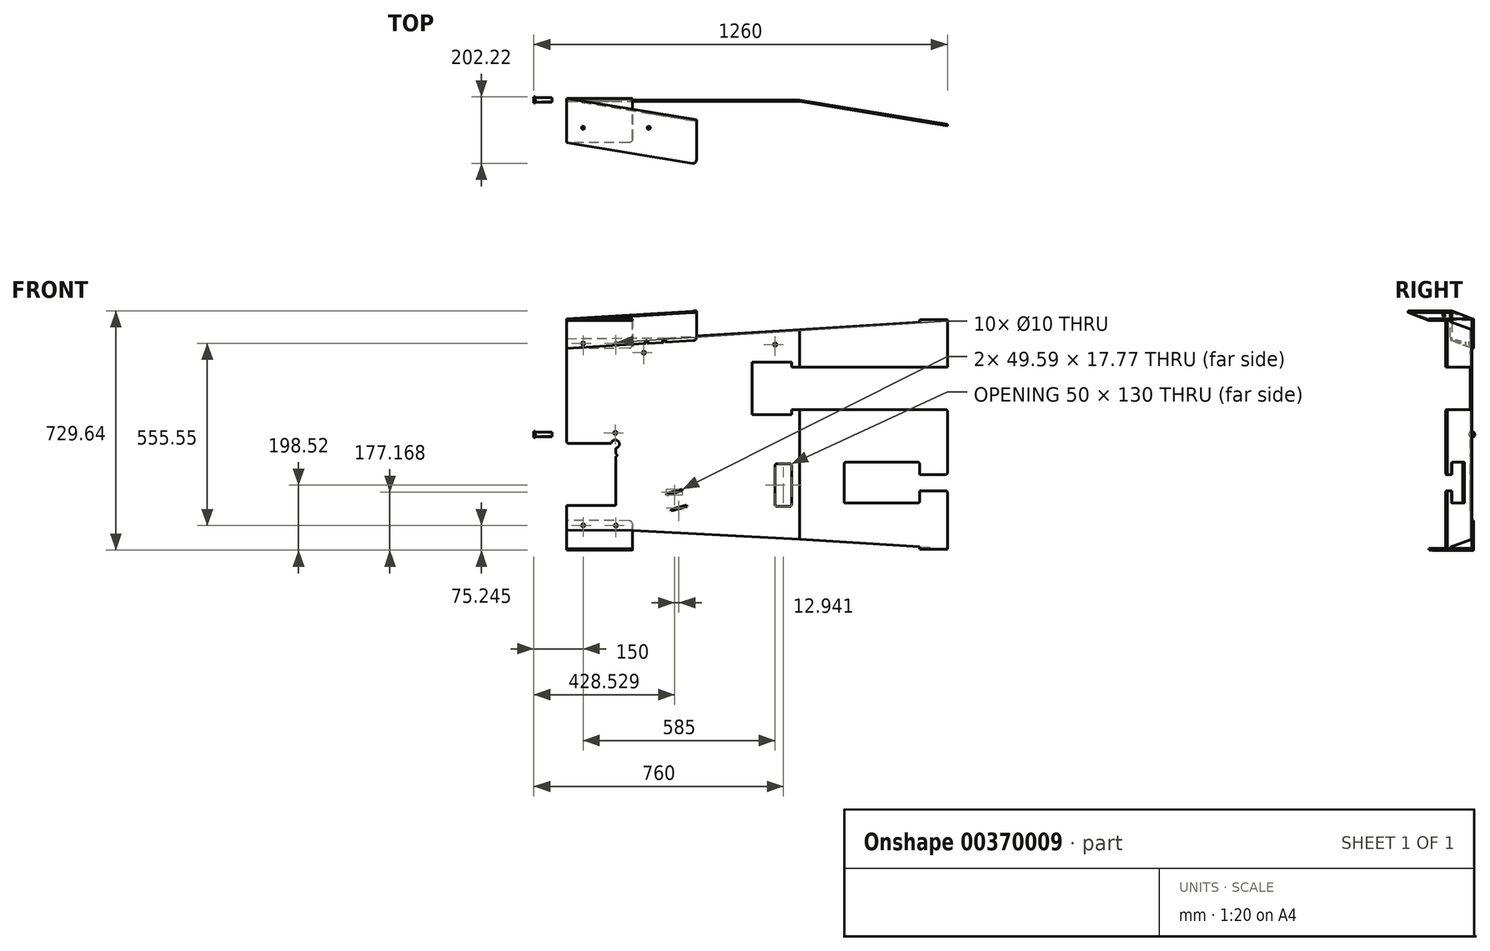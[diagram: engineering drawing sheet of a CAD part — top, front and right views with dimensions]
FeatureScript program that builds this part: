
annotation { "Feature Type Name" : "Feature", "Feature Type Description" : "" }
export const myFeature = defineFeature(function(context is Context, id is Id, definition is map)
    precondition{}
    {
        {
            var Q0;
            Q0=qCreatedBy(makeId("Front.planeOp"),FACE);
            var sketch = newSketch(context, id + "F0", { "sketchPlane" : qUnion([Q0])});
            skLineSegment(sketch, "E0", {"start": v(0, 0) * mm, "end": v(1170, 0) * mm});
            skLineSegment(sketch, "E1", {"start": v(0, 0) * mm, "end": v(0, 292) * mm});
            skPoint(sketch, "E2", {"position": v(200, 0) * mm});
            skLineSegment(sketch, "E3", {"start": v(200, 0) * mm, "end": v(200, 293) * mm});
            skPoint(sketch, "E4", {"position": v(199, 0) * mm});
            skPoint(sketch, "E5", {"position": v(302, 0) * mm});
            skLineSegment(sketch, "E6", {"start": v(302, 0) * mm, "end": v(302, 294.5) * mm});
            skPoint(sketch, "E7", {"position": v(432, 0) * mm});
            skLineSegment(sketch, "E8", {"start": v(432, 0) * mm, "end": v(432, 302.5) * mm});
            skPoint(sketch, "E9", {"position": v(565, 0) * mm});
            skLineSegment(sketch, "E10", {"start": v(565, 0) * mm, "end": v(565, 311) * mm});
            skPoint(sketch, "E11", {"position": v(710, 0) * mm});
            skLineSegment(sketch, "E12", {"start": v(710, 0) * mm, "end": v(710, 319.5) * mm});
            skPoint(sketch, "E13", {"position": v(1160, 0) * mm});
            skLineSegment(sketch, "E14", {"start": v(1160, 0) * mm, "end": v(1160, 347.5) * mm});
            skLineSegment(sketch, "E15", {"start": v(0, 292) * mm, "end": v(302, 294.5) * mm});
            skLineSegment(sketch, "E16", {"start": v(302, 294.5) * mm, "end": v(710, 319.5) * mm});
            skLineSegment(sketch, "E17", {"start": v(710, 319.5) * mm, "end": v(1160, 347.5) * mm});
            skLineSegment(sketch, "E18.MirrorCS", {"start": v(1160, 0) * mm, "end": v(1160, -347.5) * mm});
            skLineSegment(sketch, "E19.MirrorCS", {"start": v(710, 0) * mm, "end": v(710, -319.5) * mm});
            skLineSegment(sketch, "E20.MirrorCS", {"start": v(565, 0) * mm, "end": v(565, -311) * mm});
            skLineSegment(sketch, "E21.MirrorCS", {"start": v(432, 0) * mm, "end": v(432, -302.5) * mm});
            skLineSegment(sketch, "E22.MirrorCS", {"start": v(302, 0) * mm, "end": v(302, -294.5) * mm});
            skLineSegment(sketch, "E23.MirrorCS", {"start": v(200, 0) * mm, "end": v(200, -293) * mm});
            skLineSegment(sketch, "E24.MirrorCS", {"start": v(0, 0) * mm, "end": v(0, -292) * mm});
            skLineSegment(sketch, "E25", {"start": v(0, -292) * mm, "end": v(200, -293) * mm});
            skLineSegment(sketch, "E26", {"start": v(200, -293) * mm, "end": v(710, -319.5) * mm});
            skLineSegment(sketch, "E27", {"start": v(710, -319.5) * mm, "end": v(1160, -347.5) * mm});
            skSolve(sketch);
        }
        {
            var Q0;
            Q0=qCreatedBy(makeId("Front.planeOp"),FACE);
            var sketch = newSketch(context, id + "F1", { "sketchPlane" : qUnion([Q0])});
            skPoint(sketch, "E28", {"position": v(0, -217) * mm});
            skPoint(sketch, "E29", {"position": v(0, -27) * mm});
            skLineSegment(sketch, "E30", {"start": v(0, -27) * mm, "end": v(150, -27) * mm});
            skLineSegment(sketch, "E31", {"start": v(150, -27) * mm, "end": v(150, -217) * mm});
            skLineSegment(sketch, "E32", {"start": v(150, -217) * mm, "end": v(0, -217) * mm});
            skLineSegment(sketch, "E33", {"start": v(0, -27) * mm, "end": v(0, -217) * mm});
            skPoint(sketch, "E34", {"position": v(565, 310.62) * mm});
            skLineSegment(sketch, "E35", {"start": v(565, 220.62) * mm, "end": v(565, 60.62) * mm});
            skLineSegment(sketch, "E36", {"start": v(565, 220.62) * mm, "end": v(685, 220.62) * mm});
            skLineSegment(sketch, "E37", {"start": v(685, 220.62) * mm, "end": v(685, 60.62) * mm});
            skLineSegment(sketch, "E38", {"start": v(685, 60.62) * mm, "end": v(565, 60.62) * mm});
            skLineSegment(sketch, "E39", {"start": v(685, 205.62) * mm, "end": v(1160, 205.62) * mm});
            skLineSegment(sketch, "E40", {"start": v(685, 75.62) * mm, "end": v(1160, 75.62) * mm});
            skLineSegment(sketch, "E41", {"start": v(1160, 205.62) * mm, "end": v(1160, 75.62) * mm});
            skPoint(sketch, "E42", {"position": v(710, -319.5) * mm});
            skPoint(sketch, "E43", {"position": v(685, -219.5) * mm});
            skLineSegment(sketch, "E44.bottom", {"start": v(685, -219.5) * mm, "end": v(635, -219.5) * mm});
            skLineSegment(sketch, "E44.top", {"start": v(685, -89.5) * mm, "end": v(635, -89.5) * mm});
            skLineSegment(sketch, "E44.left", {"start": v(685, -219.5) * mm, "end": v(685, -89.5) * mm});
            skLineSegment(sketch, "E44.right", {"start": v(635, -219.5) * mm, "end": v(635, -89.5) * mm});
            skPoint(sketch, "E45", {"position": v(845, -209.5) * mm});
            skLineSegment(sketch, "E46", {"start": v(845, -209.5) * mm, "end": v(845, -84.5) * mm});
            skLineSegment(sketch, "E47", {"start": v(845, -84.5) * mm, "end": v(1075, -84.5) * mm});
            skLineSegment(sketch, "E48", {"start": v(1075, -84.5) * mm, "end": v(1075, -209.5) * mm});
            skLineSegment(sketch, "E49", {"start": v(1075, -209.5) * mm, "end": v(845, -209.5) * mm});
            skPoint(sketch, "E50", {"position": v(1075, -122) * mm});
            skPoint(sketch, "E51", {"position": v(1075, -147) * mm});
            skLineSegment(sketch, "E52", {"start": v(1075, -122) * mm, "end": v(1075, -172) * mm});
            skLineSegment(sketch, "E53", {"start": v(1075, -172) * mm, "end": v(1160, -172) * mm});
            skLineSegment(sketch, "E54", {"start": v(1160, -172) * mm, "end": v(1160, -122) * mm});
            skLineSegment(sketch, "E55", {"start": v(1160, -122) * mm, "end": v(1075, -122) * mm});
            skSolve(sketch);
        }
        {
            var Q0;
            Q0=qCreatedBy(makeId("Top.planeOp"),FACE);
            var sketch = newSketch(context, id + "F2", { "sketchPlane" : qUnion([Q0])});
            skPoint(sketch, "E56", {"position": v(0, 0) * mm});
            skLineSegment(sketch, "E57.0", {"start": v(302, 0) * mm, "end": v(710, 0) * mm});
            skLineSegment(sketch, "E58", {"start": v(0, 0) * mm, "end": v(710, 0) * mm});
            skLineSegment(sketch, "E59.0", {"start": v(710, 0) * mm, "end": v(1160, 0) * mm});
            skLineSegment(sketch, "E60", {"start": v(0, 0) * mm, "end": v(0, -5) * mm});
            skLineSegment(sketch, "E61", {"start": v(0, -5) * mm, "end": v(710, -5) * mm});
            skLineSegment(sketch, "E62", {"start": v(1160, -5) * mm, "end": v(1160, 0) * mm});
            skPoint(sketch, "E63", {"position": v(1160, -74) * mm});
            skLineSegment(sketch, "E64", {"start": v(1160, -79) * mm, "end": v(1160, -74) * mm});
            skLineSegment(sketch, "E65", {"start": v(710, 0) * mm, "end": v(1160, -74) * mm});
            skLineSegment(sketch, "E66", {"start": v(710, -5) * mm, "end": v(1160, -79) * mm});
            skSolve(sketch);
        }
        {
            var Q0;
            Q0 = qSketchRegion(id + "F2", true);
            extrude(context, id + "F3", {"entities" : qUnion([Q0]), "endBound" : BoundingType.SYMMETRIC, "depth" : 700 * mm});
        }
        {
            var Q0;
            Q0 = qSketchRegion(id + "F1", true);
            extrude(context, id + "F4", {"entities" : qUnion([Q0]), "operationType" : NewBodyOperationType.REMOVE, "depth" : 80 * mm});
        }
        {
            var Q0;
            Q0=qCreatedBy(makeId("Front.planeOp"),FACE);
            var sketch = newSketch(context, id + "F5", { "sketchPlane" : qUnion([Q0])});
            skLineSegment(sketch, "E67.0", {"start": v(0, 292) * mm, "end": v(302, 294.5) * mm});
            skLineSegment(sketch, "E68.0", {"start": v(302, 294.5) * mm, "end": v(710, 319.5) * mm});
            skLineSegment(sketch, "E69.0", {"start": v(710, 319.5) * mm, "end": v(1160, 347.5) * mm});
            skLineSegment(sketch, "E70.0", {"start": v(710, 350) * mm, "end": v(1160, 350) * mm});
            skLineSegment(sketch, "E71.0", {"start": v(0, 350) * mm, "end": v(710, 350) * mm});
            skLineSegment(sketch, "E72.0", {"start": v(0, 350) * mm, "end": v(0, -27) * mm});
            skLineSegment(sketch, "E73.0", {"start": v(200, -293) * mm, "end": v(710, -319.5) * mm});
            skLineSegment(sketch, "E74.0", {"start": v(0, -292) * mm, "end": v(200, -293) * mm});
            skLineSegment(sketch, "E75.0", {"start": v(710, -319.5) * mm, "end": v(1160, -347.5) * mm});
            skLineSegment(sketch, "E76.0", {"start": v(710, -350) * mm, "end": v(1160, -350) * mm});
            skLineSegment(sketch, "E77.0", {"start": v(0, -350) * mm, "end": v(710, -350) * mm});
            skLineSegment(sketch, "E78.0", {"start": v(0, -217) * mm, "end": v(0, -350) * mm});
            skLineSegment(sketch, "E79", {"start": v(1160, -347.5) * mm, "end": v(1160, -350) * mm});
            skLineSegment(sketch, "E80", {"start": v(1160, 350) * mm, "end": v(1160, 347.5) * mm});
            skSolve(sketch);
        }
        {
            var Q0;
            Q0 = qSketchRegion(id + "F5", true);
            extrude(context, id + "F6", {"entities" : qUnion([Q0]), "operationType" : NewBodyOperationType.REMOVE, "depth" : 65 * mm});
        }
        {
            var Q0;
            Q0=makeQuery(id+"F4.boolean.opBoolean","COPY",EDGE,{"derivedFrom":makeQuery(id+"F4.opExtrude","SWEPT_EDGE",EDGE,{"disambiguationData":[OSD([sQuery(id+"F1.wireOp",EDGE,"E31"),sQuery(id+"F1.wireOp",EDGE,"E32")])]})});
            var Q1;
            Q1=makeQuery(id+"F4.boolean.opBoolean","COPY",EDGE,{"derivedFrom":makeQuery(id+"F4.opExtrude","SWEPT_EDGE",EDGE,{"disambiguationData":[OSD([sQuery(id+"F1.wireOp",EDGE,"E30"),sQuery(id+"F1.wireOp",EDGE,"E31")])]})});
            var Q2;
            Q2=makeQuery(id+"F4.boolean.opBoolean","COPY",EDGE,{"derivedFrom":makeQuery(id+"F4.opExtrude","SWEPT_EDGE",EDGE,{"disambiguationData":[OSD([sQuery(id+"F1.wireOp",EDGE,"E30"),sQuery(id+"F1.wireOp",EDGE,"E33")])]})});
            var Q3;
            Q3=makeQuery(id+"F4.boolean.opBoolean","COPY",EDGE,{"derivedFrom":makeQuery(id+"F4.opExtrude","SWEPT_EDGE",EDGE,{"disambiguationData":[OSD([sQuery(id+"F1.wireOp",EDGE,"E32"),sQuery(id+"F1.wireOp",EDGE,"E33")])]})});
            var Q4;
            Q4=makeQuery(id+"F6.boolean.opBoolean","COPY",EDGE,{"derivedFrom":makeQuery(id+"F6.opExtrude","SWEPT_EDGE",EDGE,{"disambiguationData":[OSD([sQuery(id+"F5.wireOp",EDGE,"E74.0"),sQuery(id+"F5.wireOp",EDGE,"E78.0")])]})});
            var Q5;
            Q5=makeQuery(id+"F4.boolean.opBoolean","COPY",EDGE,{"derivedFrom":makeQuery(id+"F4.opExtrude","SWEPT_EDGE",EDGE,{"disambiguationData":[OSD([sQuery(id+"F1.wireOp",EDGE,"E44.top"),sQuery(id+"F1.wireOp",EDGE,"E44.left")])]})});
            var Q6;
            Q6=makeQuery(id+"F4.boolean.opBoolean","COPY",EDGE,{"derivedFrom":makeQuery(id+"F4.opExtrude","SWEPT_EDGE",EDGE,{"disambiguationData":[OSD([sQuery(id+"F1.wireOp",EDGE,"E44.top"),sQuery(id+"F1.wireOp",EDGE,"E44.right")])]})});
            var Q7;
            Q7=makeQuery(id+"F4.boolean.opBoolean","COPY",EDGE,{"derivedFrom":makeQuery(id+"F4.opExtrude","SWEPT_EDGE",EDGE,{"disambiguationData":[OSD([sQuery(id+"F1.wireOp",EDGE,"E44.bottom"),sQuery(id+"F1.wireOp",EDGE,"E44.left")])]})});
            var Q8;
            Q8=makeQuery(id+"F4.boolean.opBoolean","COPY",EDGE,{"derivedFrom":makeQuery(id+"F4.opExtrude","SWEPT_EDGE",EDGE,{"disambiguationData":[OSD([sQuery(id+"F1.wireOp",EDGE,"E44.bottom"),sQuery(id+"F1.wireOp",EDGE,"E44.right")])]})});
            var Q9;
            Q9=makeQuery(id+"F4.boolean.opBoolean","COPY",EDGE,{"derivedFrom":makeQuery(id+"F4.opExtrude","SWEPT_EDGE",EDGE,{"disambiguationData":[OSD([sQuery(id+"F1.wireOp",EDGE,"E46"),sQuery(id+"F1.wireOp",EDGE,"E49")])]})});
            var Q10;
            Q10=makeQuery(id+"F4.boolean.opBoolean","COPY",EDGE,{"derivedFrom":makeQuery(id+"F4.opExtrude","SWEPT_EDGE",EDGE,{"disambiguationData":[OSD([sQuery(id+"F1.wireOp",EDGE,"E46"),sQuery(id+"F1.wireOp",EDGE,"E47")])]})});
            var Q11;
            Q11=makeQuery(id+"F4.boolean.opBoolean","COPY",EDGE,{"derivedFrom":makeQuery(id+"F4.opExtrude","SWEPT_EDGE",EDGE,{"disambiguationData":[OSD([sQuery(id+"F1.wireOp",EDGE,"E47"),sQuery(id+"F1.wireOp",EDGE,"E48")])]})});
            var Q12;
            Q12=makeQuery(id+"F4.boolean.opBoolean","COPY",EDGE,{"derivedFrom":makeQuery(id+"F4.opExtrude","SWEPT_EDGE",EDGE,{"disambiguationData":[OSD([sQuery(id+"F1.wireOp",EDGE,"E48"),sQuery(id+"F1.wireOp",EDGE,"E49")])]})});
            var Q13;
            Q13=makeQuery(id+"F4.boolean.opBoolean","COPY",EDGE,{"derivedFrom":makeQuery(id+"F4.opExtrude","SWEPT_EDGE",EDGE,{"disambiguationData":[OSD([sQuery(id+"F1.wireOp",EDGE,"E54"),sQuery(id+"F1.wireOp",EDGE,"E55")])]})});
            var Q14;
            Q14=makeQuery(id+"F4.boolean.opBoolean","COPY",EDGE,{"derivedFrom":makeQuery(id+"F4.opExtrude","SWEPT_EDGE",EDGE,{"disambiguationData":[OSD([sQuery(id+"F1.wireOp",EDGE,"E53"),sQuery(id+"F1.wireOp",EDGE,"E54")])]})});
            var Q15;
            Q15=makeQuery(id+"F4.boolean.opBoolean","COPY",EDGE,{"derivedFrom":makeQuery(id+"F4.opExtrude","SWEPT_EDGE",EDGE,{"disambiguationData":[OSD([sQuery(id+"F1.wireOp",EDGE,"E40"),sQuery(id+"F1.wireOp",EDGE,"E41")])]})});
            var Q16;
            Q16=makeQuery(id+"F4.boolean.opBoolean","COPY",EDGE,{"derivedFrom":makeQuery(id+"F4.opExtrude","SWEPT_EDGE",EDGE,{"disambiguationData":[OSD([sQuery(id+"F1.wireOp",EDGE,"E39"),sQuery(id+"F1.wireOp",EDGE,"E41")])]})});
            var Q17;
            Q17=makeQuery(id+"F6.boolean.opBoolean","COPY",EDGE,{"derivedFrom":makeQuery(id+"F6.opExtrude","SWEPT_EDGE",EDGE,{"disambiguationData":[OSD([sQuery(id+"F5.wireOp",EDGE,"E69.0"),sQuery(id+"F5.wireOp",EDGE,"E80")])]})});
            var Q18;
            Q18=makeQuery(id+"F6.boolean.opBoolean","COPY",EDGE,{"derivedFrom":makeQuery(id+"F6.opExtrude","SWEPT_EDGE",EDGE,{"disambiguationData":[OSD([sQuery(id+"F5.wireOp",EDGE,"E75.0"),sQuery(id+"F5.wireOp",EDGE,"E79")])]})});
            fillet(context, id + "F7", {"entities" : qUnion([Q0, Q1, Q2, Q3, Q4, Q5, Q6, Q7, Q8, Q9, Q10, Q11, Q12, Q13, Q14, Q15, Q16, Q17, Q18]), "radius" : 5 * mm, "tangentPropagation" : true, "allowEdgeOverflow" : false});
        }
        {
            var Q0;
            Q0=makeQuery(id+"F3.opExtrude","SWEPT_FACE",FACE,{"disambiguationData":[OSD([sQuery(id+"F2.wireOp",EDGE,"E61")])]});
            var sketch = newSketch(context, id + "F8", { "sketchPlane" : qUnion([Q0])});
            skPoint(sketch, "E81", {"position": v(235, 249.2) * mm});
            skCircle(sketch, "E82", {"center": v(235, 249.2) * mm, "radius": 5 * mm});
            skPoint(sketch, "E83", {"position": v(635, 274.2) * mm});
            skCircle(sketch, "E84", {"center": v(635, 274.2) * mm, "radius": 5 * mm});
            skPoint(sketch, "E85", {"position": v(220, -29.3) * mm});
            skPoint(sketch, "E86", {"position": v(148, -29.3) * mm});
            skPoint(sketch, "E87", {"position": v(148, 4.7) * mm});
            skPoint(sketch, "E88", {"position": v(148, -63.3) * mm});
            skCircle(sketch, "E89", {"center": v(148, 4.7) * mm, "radius": 5 * mm});
            skCircle(sketch, "E90", {"center": v(148, -63.3) * mm, "radius": 5 * mm});
            skCircle(sketch, "E91", {"center": v(148, -29.3) * mm, "radius": 12.5 * mm});
            skSolve(sketch);
        }
        {
            var Q0;
            Q0 = qSketchRegion(id + "F8", true);
            extrude(context, id + "F9", {"entities" : qUnion([Q0]), "operationType" : NewBodyOperationType.REMOVE, "oppositeDirection" : true, "depth" : 5 * mm});
        }
        {
            var Q0;
            {var subQ2=sQuery(id+"F2.wireOp",EDGE,"E60");Q0=makeQuery(id+"F4.boolean.opBoolean","SPLIT",FACE,{"disambiguationData":[TD([makeQuery(id+"F4.opExtrude","SWEPT_FACE",FACE,{"disambiguationData":[OSD([sQuery(id+"F1.wireOp",EDGE,"E32")])]})])],"derivedFrom":makeQuery(id+"F3.opExtrude","SWEPT_FACE",FACE,{"disambiguationData":[OSD([subQ2])]})});}
            var sketch = newSketch(context, id + "F10", { "sketchPlane" : qUnion([Q0])});
            skLineSegment(sketch, "E92.0", {"start": v(5, -292.02) * mm, "end": v(0, -292.02) * mm});
            skLineSegment(sketch, "E93", {"start": v(0, -292.02) * mm, "end": v(0, -262.02) * mm});
            skLineSegment(sketch, "E94", {"start": v(0, -292.02) * mm, "end": v(0, -347.02) * mm});
            skLineSegment(sketch, "E95", {"start": v(0, -347.02) * mm, "end": v(130, -347.02) * mm});
            skLineSegment(sketch, "E96", {"start": v(130, -347.02) * mm, "end": v(130, -352.02) * mm});
            skLineSegment(sketch, "E97", {"start": v(130, -352.02) * mm, "end": v(-5, -352.02) * mm});
            skLineSegment(sketch, "E98", {"start": v(-5, -352.02) * mm, "end": v(-5, -262.02) * mm});
            skLineSegment(sketch, "E99", {"start": v(-5, -262.02) * mm, "end": v(0, -262.02) * mm});
            skLineSegment(sketch, "E100.0", {"start": v(0, -292.02) * mm, "end": v(0, -287.02) * mm});
            skSolve(sketch);
        }
        {
            var Q0;
            Q0=makeQuery(id+"F6.boolean.opBoolean","COPY",FACE,{"derivedFrom":makeQuery(id+"F6.opExtrude","SWEPT_FACE",FACE,{"disambiguationData":[OSD([sQuery(id+"F5.wireOp",EDGE,"E74.0")])]})});
            var sketch = newSketch(context, id + "F11", { "sketchPlane" : qUnion([Q0])});
            skLineSegment(sketch, "E101.0", {"start": v(6.44, 0) * mm, "end": v(201.46, 0) * mm});
            skLineSegment(sketch, "E102.0", {"start": v(6.44, 0) * mm, "end": v(1.44, 0) * mm});
            skSolve(sketch);
        }
        {
            var Q0;
            Q0=makeQuery(id+"F10.imprint","IMPRINT",FACE,{"disambiguationData":[TD([[makeQuery(id+"F10.imprint","IMPRINT",EDGE,{"derivedFrom":sQuery(id+"F10.wireOp",EDGE,"E93")}),-1.0]])]});
            var Q1;
            Q1=sQuery(id+"F11.wireOp",EDGE,"E102.0");
            var Q2;
            Q2=sQuery(id+"F11.wireOp",EDGE,"E101.0");
            sweep(context, id + "F12", {"profiles" : qUnion([Q0]), "path" : qUnion([Q1, Q2])});
        }
        {
            var Q0;
            Q0=makeQuery(id+"F12.opSweep","CAP_FACE",FACE,{"disambiguationData":[OSD([sQuery(id+"F10.wireOp",EDGE,"E93"),sQuery(id+"F10.wireOp",EDGE,"E94"),sQuery(id+"F10.wireOp",EDGE,"E95"),sQuery(id+"F10.wireOp",EDGE,"E96"),sQuery(id+"F10.wireOp",EDGE,"E97"),sQuery(id+"F10.wireOp",EDGE,"E98"),sQuery(id+"F10.wireOp",EDGE,"E99"),sQuery(id+"F10.wireOp",EDGE,"E100.0"),sQuery(id+"F11.wireOp",VERTEX,"E101.0.end")])],"isStart":false});
            var Q1;
            Q1=makeQuery(id+"F6.boolean.opBoolean","COPY",EDGE,{"derivedFrom":makeQuery(id+"F6.opExtrude","CAP_EDGE",EDGE,{"disambiguationData":[OSD([sQuery(id+"F5.wireOp",EDGE,"E73.0")])],"isStart":true})});
            var Q2;
            {var subQ8=sQuery(id+"F2.wireOp",EDGE,"E65");Q2=makeQuery(id+"F6.boolean.opBoolean","INTERSECT",EDGE,{"derivedFrom":[makeQuery(id+"F4.boolean.opBoolean","SPLIT",FACE,{"disambiguationData":[TD([makeQuery(id+"F4.opExtrude","SWEPT_FACE",FACE,{"disambiguationData":[OSD([sQuery(id+"F1.wireOp",EDGE,"E40")])]})])],"derivedFrom":makeQuery(id+"F3.opExtrude","SWEPT_FACE",FACE,{"disambiguationData":[OSD([subQ8])]})}),makeQuery(id+"F6.opExtrude","SWEPT_FACE",FACE,{"disambiguationData":[OSD([sQuery(id+"F5.wireOp",EDGE,"E75.0")])]})]});}
            sweep(context, id + "F13", {"profiles" : qUnion([Q0]), "path" : qUnion([Q1, Q2])});
        }
        {
            var Q0;
            Q0=makeQuery(id+"F13.opSweep","SWEPT_FACE",FACE,{"disambiguationData":[OSD([sQuery(id+"F2.wireOp",EDGE,"E65"),sQuery(id+"F5.wireOp",EDGE,"E75.0"),sQuery(id+"F10.wireOp",EDGE,"E98"),sQuery(id+"F11.wireOp",VERTEX,"E101.0.end")])]});
            var sketch = newSketch(context, id + "F14", { "sketchPlane" : qUnion([Q0])});
            skLineSegment(sketch, "E103", {"start": v(-1101.07, -314.71) * mm, "end": v(-1100.9, -329.71) * mm});
            skLineSegment(sketch, "E104.0", {"start": v(-196.05, -352.96) * mm, "end": v(-196.19, -262.97) * mm});
            skPoint(sketch, "E105", {"position": v(-196.16, -277.97) * mm});
            skLineSegment(sketch, "E106", {"start": v(-196.16, -277.97) * mm, "end": v(-1100.9, -329.71) * mm, "construction": true});
            skPoint(sketch, "E107", {"position": v(-1050.9, -326.85) * mm});
            skPoint(sketch, "E108", {"position": v(-800.9, -312.55) * mm});
            skPoint(sketch, "E109", {"position": v(-550.9, -298.26) * mm});
            skPoint(sketch, "E110", {"position": v(-300.9, -283.96) * mm});
            skPoint(sketch, "E111", {"position": v(-246.16, -280.83) * mm});
            skCircle(sketch, "E112", {"center": v(-1050.9, -326.85) * mm, "radius": 5 * mm});
            skCircle(sketch, "E113", {"center": v(-800.9, -312.55) * mm, "radius": 5 * mm});
            skCircle(sketch, "E114", {"center": v(-550.9, -298.26) * mm, "radius": 5 * mm});
            skCircle(sketch, "E115", {"center": v(-300.9, -283.96) * mm, "radius": 5 * mm});
            skCircle(sketch, "E116", {"center": v(-246.16, -280.83) * mm, "radius": 5 * mm});
            skSolve(sketch);
        }
        {
            var Q0;
            Q0 = qSketchRegion(id + "F14", true);
            extrude(context, id + "F15", {"entities" : qUnion([Q0]), "operationType" : NewBodyOperationType.REMOVE, "oppositeDirection" : true, "depth" : 58 * mm});
        }
        {
            var Q0;
            Q0=makeQuery(id+"F12.opSweep","SWEPT_FACE",FACE,{"disambiguationData":[OSD([sQuery(id+"F10.wireOp",EDGE,"E98"),sQuery(id+"F11.wireOp",EDGE,"E102.0")])]});
            var sketch = newSketch(context, id + "F16", { "sketchPlane" : qUnion([Q0])});
            skLineSegment(sketch, "E117.0", {"start": v(-200.02, -353.02) * mm, "end": v(-200.02, -263.02) * mm});
            skLineSegment(sketch, "E118.0", {"start": v(0, -352.02) * mm, "end": v(0, -262.02) * mm});
            skPoint(sketch, "E119", {"position": v(-200.02, -278.02) * mm});
            skPoint(sketch, "E120", {"position": v(0, -277.02) * mm});
            skLineSegment(sketch, "E121", {"start": v(-200.02, -278.02) * mm, "end": v(0, -277.02) * mm, "construction": true});
            skPoint(sketch, "E122", {"position": v(-150.02, -277.77) * mm});
            skPoint(sketch, "E123", {"position": v(-50, -277.27) * mm});
            skCircle(sketch, "E124", {"center": v(-150.02, -277.77) * mm, "radius": 5 * mm});
            skCircle(sketch, "E125", {"center": v(-50, -277.27) * mm, "radius": 5 * mm});
            skSolve(sketch);
        }
        {
            var Q0;
            Q0 = qSketchRegion(id + "F16", true);
            extrude(context, id + "F17", {"entities" : qUnion([Q0]), "operationType" : NewBodyOperationType.REMOVE, "oppositeDirection" : true, "depth" : 25 * mm});
        }
        {
            var Q0;
            Q0=makeQuery(id+"FEsiXvSyKPEOrAW_3.opPattern","COPY",EDGE,{"derivedFrom":makeQuery(id+"F12.opSweep","CAP_EDGE",EDGE,{"disambiguationData":[OSD([sQuery(id+"F10.wireOp",EDGE,"E96"),sQuery(id+"F11.wireOp",VERTEX,"E102.0.end")])],"isStart":true}),"instanceName":"1"});
            var Q1;
            Q1=makeQuery(id+"F12.opSweep","CAP_EDGE",EDGE,{"disambiguationData":[OSD([sQuery(id+"F10.wireOp",EDGE,"E96"),sQuery(id+"F11.wireOp",VERTEX,"E102.0.end")])],"isStart":true});
            var Q2;
            Q2=makeQuery(id+"F13.opSweep","CAP_EDGE",EDGE,{"disambiguationData":[OSD([sQuery(id+"F2.wireOp",EDGE,"E65"),sQuery(id+"F5.wireOp",EDGE,"E75.0"),sQuery(id+"F5.wireOp",EDGE,"E79"),sQuery(id+"F10.wireOp",EDGE,"E96"),sQuery(id+"F11.wireOp",VERTEX,"E101.0.end")])],"isStart":false});
            var Q3;
            Q3=makeQuery(id+"FWDDiy4WWACiSFN_3.opPattern","COPY",EDGE,{"derivedFrom":makeQuery(id+"F13.opSweep","CAP_EDGE",EDGE,{"disambiguationData":[OSD([sQuery(id+"F2.wireOp",EDGE,"E65"),sQuery(id+"F5.wireOp",EDGE,"E75.0"),sQuery(id+"F5.wireOp",EDGE,"E79"),sQuery(id+"F10.wireOp",EDGE,"E96"),sQuery(id+"F11.wireOp",VERTEX,"E101.0.end")])],"isStart":false}),"instanceName":"1"});
            var Q4;
            Q4=makeQuery(id+"FWDDiy4WWACiSFN_3.opPattern","COPY",EDGE,{"derivedFrom":makeQuery(id+"F13.opSweep","CAP_EDGE",EDGE,{"disambiguationData":[OSD([sQuery(id+"F2.wireOp",EDGE,"E65"),sQuery(id+"F5.wireOp",EDGE,"E75.0"),sQuery(id+"F5.wireOp",EDGE,"E79"),sQuery(id+"F10.wireOp",EDGE,"E99"),sQuery(id+"F11.wireOp",VERTEX,"E101.0.end")])],"isStart":false}),"instanceName":"1"});
            var Q5;
            Q5=makeQuery(id+"FEsiXvSyKPEOrAW_3.opPattern","COPY",EDGE,{"derivedFrom":makeQuery(id+"F12.opSweep","CAP_EDGE",EDGE,{"disambiguationData":[OSD([sQuery(id+"F10.wireOp",EDGE,"E99"),sQuery(id+"F11.wireOp",VERTEX,"E102.0.end")])],"isStart":true}),"instanceName":"1"});
            var Q6;
            Q6=makeQuery(id+"F12.opSweep","CAP_EDGE",EDGE,{"disambiguationData":[OSD([sQuery(id+"F10.wireOp",EDGE,"E99"),sQuery(id+"F11.wireOp",VERTEX,"E102.0.end")])],"isStart":true});
            var Q7;
            Q7=makeQuery(id+"F13.opSweep","CAP_EDGE",EDGE,{"disambiguationData":[OSD([sQuery(id+"F2.wireOp",EDGE,"E65"),sQuery(id+"F5.wireOp",EDGE,"E75.0"),sQuery(id+"F5.wireOp",EDGE,"E79"),sQuery(id+"F10.wireOp",EDGE,"E99"),sQuery(id+"F11.wireOp",VERTEX,"E101.0.end")])],"isStart":false});
            fillet(context, id + "F18", {"entities" : qUnion([Q0, Q1, Q2, Q3, Q4, Q5, Q6, Q7]), "radius" : 10 * mm, "tangentPropagation" : true, "allowEdgeOverflow" : false});
        }
        {
            var Q0;
            Q0=qCreatedBy(makeId("Top.planeOp"),FACE);
            cPlane(context, id + "F19", {"entities" : qUnion([Q0]), "cplaneType" : CPlaneType.OFFSET, "offset" : 410 * mm, "oppositeDirection" : true, "width" : 150 * mm, "height" : 150 * mm});
        }
        {
            var Q0;
            Q0=qCreatedBy(id+"F19.planeOp",FACE);
            var sketch = newSketch(context, id + "F20", { "sketchPlane" : qUnion([Q0])});
            skLineSegment(sketch, "E126.0", {"start": v(0, -120) * mm, "end": v(0, 5) * mm});
            skLineSegment(sketch, "E127.0", {"start": v(200.02, -130) * mm, "end": v(200.02, 5) * mm});
            skLineSegment(sketch, "E128.0", {"start": v(707, 5) * mm, "end": v(696, -130) * mm});
            skLineSegment(sketch, "E129.0", {"start": v(1085.24, -183.87) * mm, "end": v(1105.46, -60.53) * mm});
            skPoint(sketch, "E130", {"position": v(0, -85) * mm});
            skPoint(sketch, "E131", {"position": v(200.02, -85) * mm});
            skPoint(sketch, "E132", {"position": v(699.67, -85) * mm});
            skPoint(sketch, "E133", {"position": v(1090.7, -150.53) * mm});
            skLineSegment(sketch, "E134", {"start": v(0, -85) * mm, "end": v(200.02, -85) * mm, "construction": true});
            skLineSegment(sketch, "E135", {"start": v(200.02, -85) * mm, "end": v(699.67, -85) * mm, "construction": true});
            skLineSegment(sketch, "E136", {"start": v(699.67, -85) * mm, "end": v(1090.7, -150.53) * mm, "construction": true});
            skPoint(sketch, "E137", {"position": v(50, -85) * mm});
            skPoint(sketch, "E138", {"position": v(250, -85) * mm});
            skPoint(sketch, "E139", {"position": v(450, -85) * mm});
            skPoint(sketch, "E140", {"position": v(650, -85) * mm});
            skPoint(sketch, "E141", {"position": v(850, -110.2) * mm});
            skPoint(sketch, "E142", {"position": v(1050, -143.7) * mm});
            skCircle(sketch, "E143", {"center": v(50, -85) * mm, "radius": 5 * mm});
            skCircle(sketch, "E144", {"center": v(250, -85) * mm, "radius": 5 * mm});
            skCircle(sketch, "E145", {"center": v(450, -85) * mm, "radius": 5 * mm});
            skCircle(sketch, "E146", {"center": v(650, -85) * mm, "radius": 5 * mm});
            skCircle(sketch, "E147", {"center": v(850, -110.2) * mm, "radius": 5 * mm});
            skCircle(sketch, "E148", {"center": v(1050, -143.7) * mm, "radius": 5 * mm});
            skSolve(sketch);
        }
        {
            var Q0;
            Q0 = qSketchRegion(id + "F20", true);
            extrude(context, id + "F21", {"entities" : qUnion([Q0]), "operationType" : NewBodyOperationType.REMOVE, "depth" : 100 * mm});
        }
        {
            var Q0;
            Q0=qCreatedBy(makeId("Front.planeOp"),FACE);
            var sketch = newSketch(context, id + "F22", { "sketchPlane" : qUnion([Q0])});
            skPoint(sketch, "E149", {"position": v(-100, 0) * mm});
            skLineSegment(sketch, "E150", {"start": v(-100, 0) * mm, "end": v(-45, 0) * mm});
            skLineSegment(sketch, "E151", {"start": v(-45, 0) * mm, "end": v(-45, 7) * mm});
            skLineSegment(sketch, "E152", {"start": v(-45, 7) * mm, "end": v(-100, 7) * mm});
            skLineSegment(sketch, "E153", {"start": v(-100, 7) * mm, "end": v(-100, 0) * mm});
            skPoint(sketch, "E154", {"position": v(-45, 5) * mm});
            skLineSegment(sketch, "E155", {"start": v(-45, 5) * mm, "end": v(-100, 5) * mm});
            skPoint(sketch, "E155.endSnap0", {"position": v(-100, 3.5) * mm});
            skPoint(sketch, "E156", {"position": v(-100, 9) * mm});
            skLineSegment(sketch, "E157", {"start": v(-100, 9) * mm, "end": v(-100, 7) * mm});
            skLineSegment(sketch, "E158", {"start": v(-100, 9) * mm, "end": v(-95, 9) * mm});
            skLineSegment(sketch, "E159", {"start": v(-95, 9) * mm, "end": v(-95, 7) * mm});
            skSolve(sketch);
        }
        {
            var Q0;
            {var subQ0=sQuery(id+"F22.wireOp",EDGE,"E157");Q0=makeQuery(id+"F22.imprint","IMPRINT",FACE,{"disambiguationData":[TD([[makeQuery(id+"F22.imprint","IMPRINT",EDGE,{"derivedFrom":subQ0}),1.0]])]});}
            var Q1;
            {var subQ3=sQuery(id+"F22.wireOp",EDGE,"E155");Q1=makeQuery(id+"F22.imprint","IMPRINT",FACE,{"disambiguationData":[TD([[makeQuery(id+"F22.imprint","IMPRINT",EDGE,{"derivedFrom":subQ3}),-1.0]])]});}
            var Q2;
            Q2=sQuery(id+"F22.wireOp",EDGE,"E150");
            revolve(context, id + "F23", {"entities" : qUnion([Q0, Q1]), "axis" : qUnion([Q2]), "revolveType" : RevolveType.FULL});
        }
        {
            var Q0;
            Q0=makeQuery(id+"F3.opExtrude","SWEPT_FACE",FACE,{"disambiguationData":[OSD([sQuery(id+"F2.wireOp",EDGE,"E61")])]});
            var sketch = newSketch(context, id + "F24", { "sketchPlane" : qUnion([Q0])});
            skLineSegment(sketch, "E160", {"start": v(353.32, -171.8) * mm, "end": v(305.03, -184.74) * mm});
            skLineSegment(sketch, "E161", {"start": v(305.03, -184.74) * mm, "end": v(303.73, -179.9) * mm});
            skLineSegment(sketch, "E162", {"start": v(303.73, -179.9) * mm, "end": v(352.03, -166.97) * mm});
            skLineSegment(sketch, "E163", {"start": v(352.03, -166.97) * mm, "end": v(353.32, -171.8) * mm});
            skLineSegment(sketch, "E164", {"start": v(366.27, -220.1) * mm, "end": v(317.97, -233.03) * mm});
            skLineSegment(sketch, "E165", {"start": v(317.97, -233.03) * mm, "end": v(316.68, -228.2) * mm});
            skLineSegment(sketch, "E166", {"start": v(316.68, -228.2) * mm, "end": v(364.97, -215.26) * mm});
            skLineSegment(sketch, "E167", {"start": v(364.97, -215.26) * mm, "end": v(366.27, -220.1) * mm});
            skPoint(sketch, "E168", {"position": v(340.82, -221.73) * mm});
            skPoint(sketch, "E169", {"position": v(329.18, -178.27) * mm});
            skLineSegment(sketch, "E170", {"start": v(329.18, -178.27) * mm, "end": v(340.82, -221.73) * mm, "construction": true});
            skPoint(sketch, "E171", {"position": v(335, -200) * mm});
            skPoint(sketch, "E172", {"position": v(235, 249.2) * mm});
            skSolve(sketch);
        }
        {
            var Q0;
            Q0 = qSketchRegion(id + "F24", true);
            extrude(context, id + "F25", {"entities" : qUnion([Q0]), "operationType" : NewBodyOperationType.REMOVE, "oppositeDirection" : true, "depth" : 25 * mm});
        }
        {
            var Q0;
            Q0=makeQuery(id+"F12.opSweep","SWEPT_BODY",BODY,{"disambiguationData":[OSD([sQuery(id+"F10.wireOp",EDGE,"E93"),sQuery(id+"F10.wireOp",EDGE,"E94"),sQuery(id+"F10.wireOp",EDGE,"E95"),sQuery(id+"F10.wireOp",EDGE,"E96"),sQuery(id+"F10.wireOp",EDGE,"E97"),sQuery(id+"F10.wireOp",EDGE,"E98"),sQuery(id+"F10.wireOp",EDGE,"E99"),sQuery(id+"F10.wireOp",EDGE,"E100.0"),sQuery(id+"F11.wireOp",EDGE,"E101.0")])]});
            var Q1;
            Q1=qCreatedBy(makeId("Top.planeOp"),FACE);
            mirror(context, id + "F29", {"entities" : qUnion([Q0]), "mirrorPlane" : qUnion([Q1])});
        }
        {
            var Q0;
            Q0=makeQuery(id+"F13.opSweep","SWEPT_BODY",BODY,{"disambiguationData":[OSD([sQuery(id+"F2.wireOp",EDGE,"E65"),sQuery(id+"F5.wireOp",EDGE,"E75.0"),sQuery(id+"F10.wireOp",EDGE,"E93"),sQuery(id+"F10.wireOp",EDGE,"E94"),sQuery(id+"F10.wireOp",EDGE,"E95"),sQuery(id+"F10.wireOp",EDGE,"E96"),sQuery(id+"F10.wireOp",EDGE,"E97"),sQuery(id+"F10.wireOp",EDGE,"E98"),sQuery(id+"F10.wireOp",EDGE,"E99"),sQuery(id+"F10.wireOp",EDGE,"E100.0"),sQuery(id+"F11.wireOp",VERTEX,"E101.0.end")])]});
            var Q1;
            Q1=qCreatedBy(makeId("Top.planeOp"),FACE);
            mirror(context, id + "F30", {"entities" : qUnion([Q0]), "mirrorPlane" : qUnion([Q1])});
        }
        {
            var Q0;
            Q0=makeQuery(id+"F13.opSweep","SWEPT_BODY",BODY,{"disambiguationData":[OSD([sQuery(id+"F2.wireOp",EDGE,"E65"),sQuery(id+"F5.wireOp",EDGE,"E75.0"),sQuery(id+"F10.wireOp",EDGE,"E93"),sQuery(id+"F10.wireOp",EDGE,"E94"),sQuery(id+"F10.wireOp",EDGE,"E95"),sQuery(id+"F10.wireOp",EDGE,"E96"),sQuery(id+"F10.wireOp",EDGE,"E97"),sQuery(id+"F10.wireOp",EDGE,"E98"),sQuery(id+"F10.wireOp",EDGE,"E99"),sQuery(id+"F10.wireOp",EDGE,"E100.0"),sQuery(id+"F11.wireOp",VERTEX,"E101.0.end")])]});
            deleteBodies(context, id + "F31", {"entities" : qUnion([Q0])});
        }
    });
